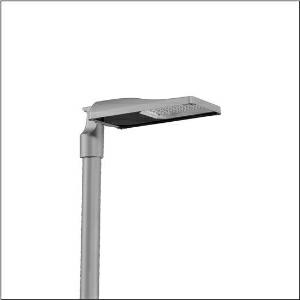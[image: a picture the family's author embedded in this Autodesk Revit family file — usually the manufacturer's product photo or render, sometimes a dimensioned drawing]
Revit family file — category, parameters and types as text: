
# Revit family: streetlight_sl_31_mini___st1_0a_5xh2d3ab08ja_f81c
name_source: partatom
category: Lighting Fixtures
units: mm (PartAtom-declared; Revit-internal decimal feet)

## family parameters
Cut with Voids When Loaded = No
Host = Face
Light Source = No
Part Type = Normal
Room Calculation Point = No
Round Connector Dimension = Use Diameter
Shared = No

## types (1)
- --- (1 x LED, 12140 lm, 81.1 W, 3000K)
    Apparent Load = 81 VA
    CIE Flux Codes = 40 73 97 100 100
    Color Rendering = 70
    Color Temperature = 3000K
    Default Elevation = 1800 mm
    Description = Streetlight SL 31 mini Easy LST mast luminaire for post-top, side-entry; light control with lens of PMMA; light distribution: ST1.0a, direct asymmetric distribution, for standard-compliant lighting for roads and squares; LED: luminous flux: 12.140lm, light colour: 730, colour temperature: 3000K; luminous efficacy: 149,7lm/W; control: pre-setting: linear dimming characteristic, flexible luminous flux parameterisation, time-dependent luminous flux control, constant luminous flux control, power reduction, intelligent temperature release in ECG and LED module, overheat protection; luminaire housing, of diecast aluminium, Siteco® metallic grey (DB 702S), corrosivity category C5 high according to DIN EN ISO 12944; cover of toughened safety glass, transparent, mast flange of diecast aluminium, Siteco® metallic grey (DB 702S), spigot size: 76/60mm, mast flange included unmounted; with cable H07RN-F 3x 1.5mm², cable length: 10,5m, connection cable pre-assembled; mains connection: 220..240V, AC, 50/60Hz; power consumption (at start of service life): 81,1W / (at end of service life): 88,3W / (with reduced operation 50%): 36,4W; protection rating (complete): IP66; insulation class (complete): insulation class II (safety insulation); impact resistance: IK10; certification: CE, ENEC, ENEC+, VDE, UKCA; permissible operating ambient temperature for outdoor applications: -40..+50°C; packaging unit: 1 piece

Light Distribution: ST1.0a
    Height = 76 mm
    Lamp = 1 x LED
    Lamp Light Flux = 12140 lm
    Lamp Power = 81.1 W
    Lamp count = 1
    Length = 547 mm
    Luminous efficacy = 150 lm/W
    Manufacturer = Siteco
    ModVariant = No
    Model = 5XH2D3AB08JA
    Number of Poles = 1
    OnlyDefault = Yes
    Power Factor = 1
    Product Name = Streetlight SL 31 mini | ST1.0a
    Product group = mast luminaire | pylon top
    ProductGroupID = 6100
    Protection Class = Protection class II
    Protection Degree = IP 66
    RLX_Detail_Level = 1
    RLX_Emergency_Light_Flux = 0 lm
    RLX_Emergency_Type = 0
    RLX_Emergency_Type_DB = No
    RlxData = <blob elided: 39801 chars, md5=d14148bc>
    Socket = socket
    Standby Power = 0 W
    System Light Flux = 12140 lm
    System Power = 81 W
    Type Comments = factory setting: luminous flux: 100 % | dim-lin: 254 | 860 mA
    Type Image = l_1300326.jpg
    URL = http://relux.com
    VarID = @adj_071517
    Voltage = 0 V
    Weight = 0.00 kg
    Width = 265 mm

## geometry (parser evidence)
native form markers: Blend x4, Sweep x8
no freeform markers — native parametric forms only
